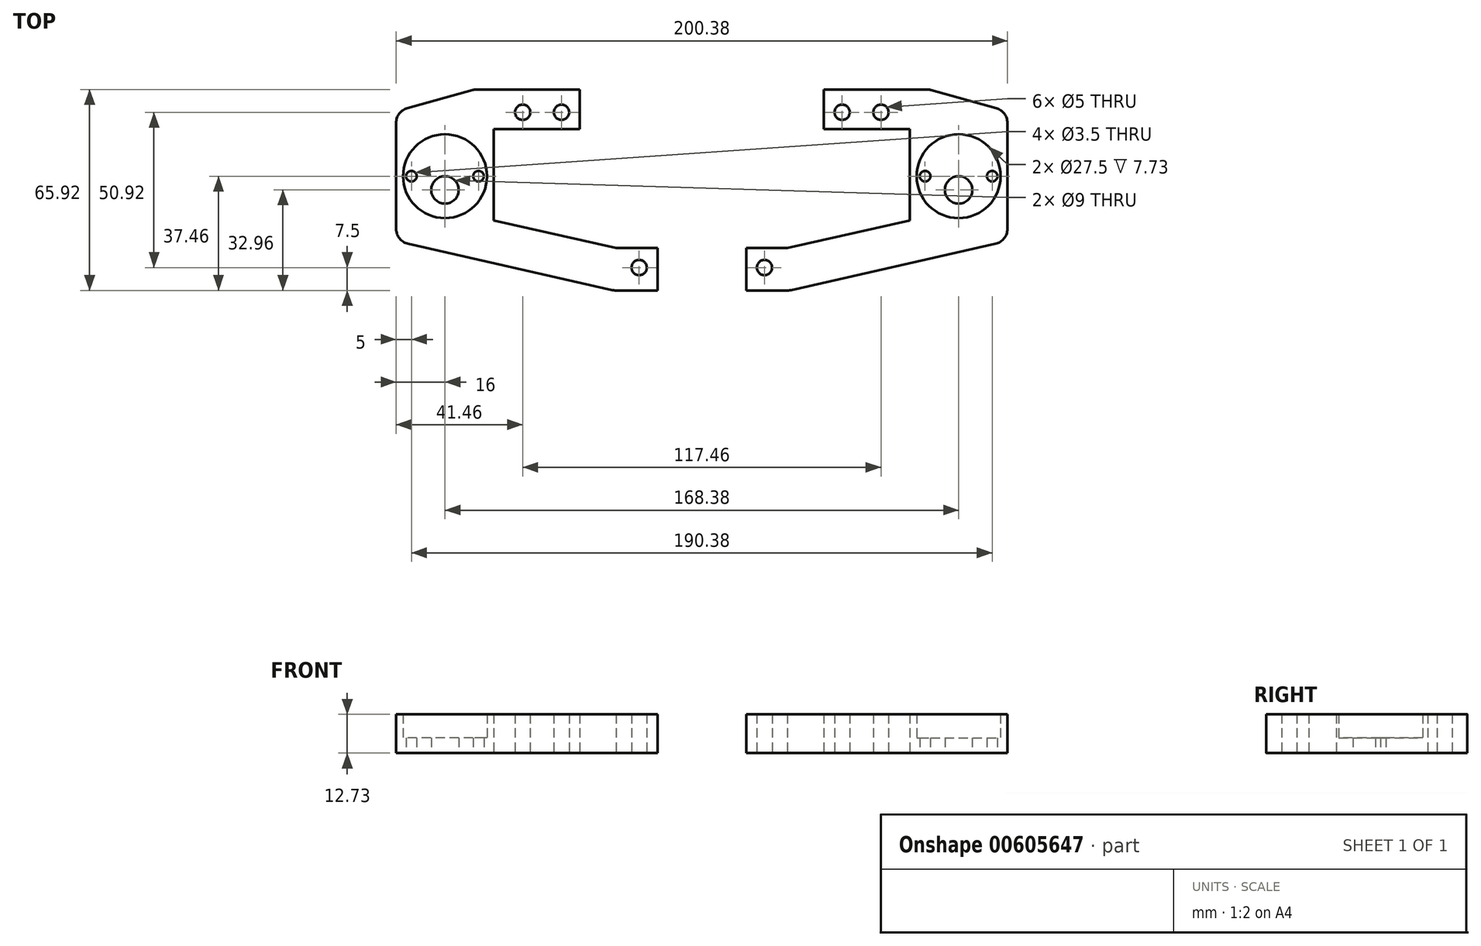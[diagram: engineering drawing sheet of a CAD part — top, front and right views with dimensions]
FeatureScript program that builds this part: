
annotation { "Feature Type Name" : "Feature", "Feature Type Description" : "" }
export const myFeature = defineFeature(function(context is Context, id is Id, definition is map)
    precondition{}
    {
        {
            var Q0;
            Q0=qCreatedBy(makeId("Top.planeOp"),FACE);
            var sketch = newSketch(context, id + "F0", { "sketchPlane" : qUnion([Q0])});
            skPoint(sketch, "E0", {"position": v(0, 0) * mm});
            skPoint(sketch, "E1", {"position": v(0, -50.92) * mm});
            skPoint(sketch, "E2", {"position": v(25.46, -50.92) * mm});
            skPoint(sketch, "E3", {"position": v(-12.73, 0) * mm});
            skPoint(sketch, "E4", {"position": v(0, -25.46) * mm});
            skPoint(sketch, "E5", {"position": v(-38.2, -25.46) * mm});
            skPoint(sketch, "E6.start.orphan", {"position": v(6, 0) * mm});
            skLineSegment(sketch, "E7", {"start": v(6, 5.5) * mm, "end": v(6, -5.5) * mm});
            skLineSegment(sketch, "E8", {"start": v(31.46, -44.53) * mm, "end": v(17.95, -44.53) * mm});
            skCircle(sketch, "E9", {"center": v(-12.73, 0) * mm, "radius": 2.5 * mm});
            skCircle(sketch, "E10", {"center": v(0, 0) * mm, "radius": 2.5 * mm});
            skCircle(sketch, "E11", {"center": v(25.46, -50.92) * mm, "radius": 2.5 * mm});
            skPoint(sketch, "E12", {"position": v(6, 7.5) * mm});
            skLineSegment(sketch, "E13", {"start": v(6, 7.5) * mm, "end": v(6, 5.5) * mm});
            skLineSegment(sketch, "E14", {"start": v(17.2, -58.42) * mm, "end": v(31.46, -58.42) * mm});
            skPoint(sketch, "E15", {"position": v(31.46, -50.92) * mm});
            skLineSegment(sketch, "E16", {"start": v(31.46, -44.53) * mm, "end": v(31.46, -58.42) * mm});
            skPoint(sketch, "E17", {"position": v(31.46, -44.53) * mm});
            skPoint(sketch, "E18", {"position": v(31.46, -58.42) * mm});
            skLineSegment(sketch, "E19.2", {"start": v(-28.69, -33.96) * mm, "end": v(-28.69, -33.83) * mm});
            skLineSegment(sketch, "E20", {"start": v(-22.2, -35.43) * mm, "end": v(17.95, -44.53) * mm});
            skLineSegment(sketch, "E21", {"start": v(6, 7.5) * mm, "end": v(-28.42, 7.5) * mm});
            skCircle(sketch, "E22", {"center": v(-38.2, -25.46) * mm, "radius": 4.5 * mm});
            skCircle(sketch, "E23", {"center": v(-49.19, -20.96) * mm, "radius": 1.75 * mm});
            skCircle(sketch, "E24", {"center": v(-27.2, -20.96) * mm, "radius": 1.75 * mm});
            skCircle(sketch, "E25", {"center": v(-38.2, -20.96) * mm, "radius": 13.75 * mm});
            skCircle(sketch, "E26", {"center": v(-38.2, -20.96) * mm, "radius": 16 * mm});
            skLineSegment(sketch, "E27", {"start": v(-22.19, -20.96) * mm, "end": v(-22.2, -35.43) * mm});
            skLineSegment(sketch, "E28", {"start": v(-22.2, -20.96) * mm, "end": v(-22.2, -5.5) * mm});
            skLineSegment(sketch, "E29", {"start": v(-22.2, -5.5) * mm, "end": v(6, -5.5) * mm});
            skLineSegment(sketch, "E30", {"start": v(-54.2, -20.96) * mm, "end": v(-54.2, 0.32) * mm});
            skLineSegment(sketch, "E31", {"start": v(-54.2, -20.96) * mm, "end": v(-54.2, -42.24) * mm});
            skLineSegment(sketch, "E32", {"start": v(17.2, -58.42) * mm, "end": v(-54.2, -42.24) * mm});
            skPoint(sketch, "E33", {"position": v(-54.19, 0.32) * mm});
            skLineSegment(sketch, "E34", {"start": v(-28.42, 7.5) * mm, "end": v(-54.19, 0.32) * mm});
            skPoint(sketch, "E35.start.orphan", {"position": v(-22.2, 7.5) * mm});
            skSolve(sketch);
        }
        {
            var Q0;
            Q0=makeQuery(id+"F0.imprint","IMPRINT",FACE,{"disambiguationData":[TD([[makeQuery(id+"F0.imprint","IMPRINT",EDGE,{"derivedFrom":sQuery(id+"F0.wireOp",EDGE,"E7")}),-1.0]])]});
            var Q1;
            Q1=makeQuery(id+"F0.imprint","IMPRINT",FACE,{"disambiguationData":[TD([[makeQuery(id+"F0.imprint","IMPRINT",EDGE,{"derivedFrom":sQuery(id+"F0.wireOp",EDGE,"E8")}),1.0]])]});
            var Q2;
            Q2=makeQuery(id+"F0.imprint","IMPRINT",FACE,{"disambiguationData":[TD([[makeQuery(id+"F0.imprint","IMPRINT",EDGE,{"derivedFrom":sQuery(id+"F0.wireOp",EDGE,"E25")}),-1.0]])]});
            extrude(context, id + "F1", {"entities" : qUnion([Q0, Q1, Q2]), "depth" : 12.73 * mm, "offsetDistance" : 25 * mm});
        }
        {
            var Q0;
            Q0=makeQuery(id+"F0.imprint","IMPRINT",FACE,{"disambiguationData":[TD([[makeQuery(id+"F0.imprint","IMPRINT",EDGE,{"derivedFrom":sQuery(id+"F0.wireOp",EDGE,"E22")}),-1.0]])]});
            extrude(context, id + "F2", {"entities" : qUnion([Q0]), "operationType" : NewBodyOperationType.ADD, "depth" : 5 * mm, "offsetDistance" : 25 * mm});
        }
        {
            var Q0;
            Q0=makeQuery(id+"F1.opExtrude","SWEPT_EDGE",EDGE,{"disambiguationData":[OSD([sQuery(id+"F0.wireOp",EDGE,"E30"),sQuery(id+"F0.wireOp",EDGE,"E34")])]});
            var Q1;
            Q1=makeQuery(id+"F1.opExtrude","SWEPT_EDGE",EDGE,{"disambiguationData":[OSD([sQuery(id+"F0.wireOp",EDGE,"E21"),sQuery(id+"F0.wireOp",EDGE,"E34")])]});
            var Q2;
            Q2=makeQuery(id+"F1.opExtrude","SWEPT_EDGE",EDGE,{"disambiguationData":[OSD([sQuery(id+"F0.wireOp",EDGE,"E31"),sQuery(id+"F0.wireOp",EDGE,"E32")])]});
            var Q3;
            Q3=makeQuery(id+"F1.opExtrude","SWEPT_EDGE",EDGE,{"disambiguationData":[OSD([sQuery(id+"F0.wireOp",EDGE,"E14"),sQuery(id+"F0.wireOp",EDGE,"E32")])]});
            fillet(context, id + "F3", {"entities" : qUnion([Q0, Q1, Q2, Q3]), "radius" : 5 * mm, "tangentPropagation" : true, "allowEdgeOverflow" : false});
        }
        {
            var Q0;
            Q0=makeQuery(id+"F1.opExtrude","SWEPT_BODY",BODY,{"disambiguationData":[OSD([sQuery(id+"F0.wireOp",EDGE,"E7"),sQuery(id+"F0.wireOp",EDGE,"E8"),sQuery(id+"F0.wireOp",EDGE,"E9"),sQuery(id+"F0.wireOp",EDGE,"E10"),sQuery(id+"F0.wireOp",EDGE,"E11"),sQuery(id+"F0.wireOp",EDGE,"E13"),sQuery(id+"F0.wireOp",EDGE,"E14"),sQuery(id+"F0.wireOp",EDGE,"E16"),sQuery(id+"F0.wireOp",EDGE,"E20"),sQuery(id+"F0.wireOp",EDGE,"E21"),sQuery(id+"F0.wireOp",EDGE,"E25"),sQuery(id+"F0.wireOp",EDGE,"E27"),sQuery(id+"F0.wireOp",EDGE,"E28"),sQuery(id+"F0.wireOp",EDGE,"E29"),sQuery(id+"F0.wireOp",EDGE,"E30"),sQuery(id+"F0.wireOp",EDGE,"E31"),sQuery(id+"F0.wireOp",EDGE,"E32"),sQuery(id+"F0.wireOp",EDGE,"E34")])]});
            transform(context, id + "F4", {"entities" : qUnion([Q0]), "transformType" : TransformType.TRANSLATION_3D, "dx" : -46 * mm, "dy" : 0 * mm, "dz" : 0 * mm, "makeCopy" : false});
        }
        {
            var Q0;
            Q0=makeQuery(id+"F1.opExtrude","SWEPT_BODY",BODY,{"disambiguationData":[OSD([sQuery(id+"F0.wireOp",EDGE,"E7"),sQuery(id+"F0.wireOp",EDGE,"E8"),sQuery(id+"F0.wireOp",EDGE,"E9"),sQuery(id+"F0.wireOp",EDGE,"E10"),sQuery(id+"F0.wireOp",EDGE,"E11"),sQuery(id+"F0.wireOp",EDGE,"E13"),sQuery(id+"F0.wireOp",EDGE,"E14"),sQuery(id+"F0.wireOp",EDGE,"E16"),sQuery(id+"F0.wireOp",EDGE,"E20"),sQuery(id+"F0.wireOp",EDGE,"E21"),sQuery(id+"F0.wireOp",EDGE,"E25"),sQuery(id+"F0.wireOp",EDGE,"E27"),sQuery(id+"F0.wireOp",EDGE,"E28"),sQuery(id+"F0.wireOp",EDGE,"E29"),sQuery(id+"F0.wireOp",EDGE,"E30"),sQuery(id+"F0.wireOp",EDGE,"E31"),sQuery(id+"F0.wireOp",EDGE,"E32"),sQuery(id+"F0.wireOp",EDGE,"E34")])]});
            var Q1;
            Q1=qCreatedBy(makeId("Right.planeOp"),FACE);
            mirror(context, id + "F5", {"entities" : qUnion([Q0]), "mirrorPlane" : qUnion([Q1])});
        }
    });
